# Revit family: P190780JX-213c_JKCPL181GL_StainlessSteel_JA_Refrigeration_Columns
name_source: partatom
category: Specialty Equipment
units: mm (PartAtom-declared; Revit-internal decimal feet)

## family parameters
Always vertical = Yes
Cut with Voids When Loaded = No
Enable Cutting in Views = No
Maintain Annotation Orientation = No
Part Type = Normal
Room Calculation Point = No
Round Connector Dimension = Use Diameter
Shared = No
Work Plane-Based = No

## types (1)
- JKCPL181GL
    Accent Material = ARCAT - Metal - Steel - Black
    Amps = 0 A
    Body Material = ARCAT - Metal - Steel - Stainless
    Clearance Material = ARCAT - Clearance
    Default Elevation = 0"
    Depth = 26 5/8"
    Door Material = ARCAT - Metal - Steel - Stainless
    Family Name = 18" Column Panel Kits - JBZFL18IGX
    Handle Material = ARCAT - Metal - Steel - Gray
    Height = 83 7/16"
    Manufacturer = Jenn Air
    Model = JKCPL181GL
    Voltage = 0 V
    Wheel Material = ARCAT - Plastic - Black
    Width = 17 3/4"

## geometry (parser evidence)
native form markers: Sweep x2
no freeform markers — native parametric forms only
